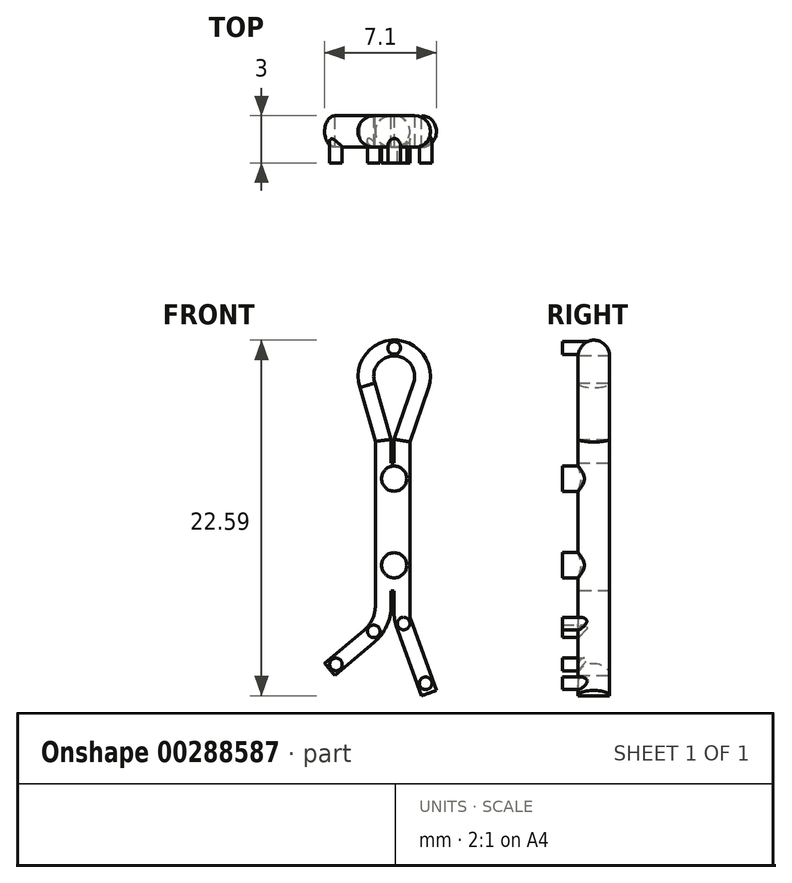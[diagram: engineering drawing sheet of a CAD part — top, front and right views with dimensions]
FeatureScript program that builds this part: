
annotation { "Feature Type Name" : "Feature", "Feature Type Description" : "" }
export const myFeature = defineFeature(function(context is Context, id is Id, definition is map)
    precondition{}
    {
        {
            var Q0;
            Q0=qCreatedBy(makeId("Top.planeOp"),FACE);
            var sketch = newSketch(context, id + "F0", { "sketchPlane" : qUnion([Q0])});
            skLineSegment(sketch, "E0", {"start": v(0, -1) * mm, "end": v(0, 1) * mm});
            skArc(sketch, "E1", {"start": v(0, -1) * mm, "mid": v(1, 0) * mm, "end": v(0, 1) * mm});
            skSolve(sketch);
        }
        {
            var Q0;
            Q0=qCreatedBy(makeId("Front.planeOp"),FACE);
            var sketch = newSketch(context, id + "F1", { "sketchPlane" : qUnion([Q0])});
            skLineSegment(sketch, "E2", {"start": v(0, 0) * mm, "end": v(0, 10) * mm});
            skLineSegment(sketch, "E3", {"start": v(0, 10) * mm, "end": v(1.23, 13.58) * mm});
            skLineSegment(sketch, "E4", {"start": v(-1.23, 13.58) * mm, "end": v(-0.2, 10) * mm});
            skLineSegment(sketch, "E5", {"start": v(-0.2, 10) * mm, "end": v(-0.2, 0) * mm});
            skArc(sketch, "E6", {"start": v(1.23, 13.58) * mm, "mid": v(0, 15.3) * mm, "end": v(-1.23, 13.58) * mm});
            skSolve(sketch);
        }
        {
            var Q0;
            Q0=makeQuery(id+"F0.imprint","IMPRINT",FACE,{"disambiguationData":[TD([[makeQuery(id+"F0.imprint","IMPRINT",EDGE,{"derivedFrom":sQuery(id+"F0.wireOp",EDGE,"E0")}),-1.0]])]});
            var Q1;
            Q1=sQuery(id+"F1.wireOp",EDGE,"E2");
            var Q2;
            Q2=sQuery(id+"F1.wireOp",EDGE,"E3");
            var Q3;
            Q3=sQuery(id+"F1.wireOp",EDGE,"E6");
            var Q4;
            Q4=sQuery(id+"F1.wireOp",EDGE,"E4");
            var Q5;
            Q5=sQuery(id+"F1.wireOp",EDGE,"E5");
            sweep(context, id + "F2", {"profiles" : qUnion([Q0]), "path" : qUnion([Q1, Q2, Q3, Q4, Q5])});
        }
        {
            var Q0;
            Q0=qCreatedBy(makeId("Front.planeOp"),FACE);
            var sketch = newSketch(context, id + "F3", { "sketchPlane" : qUnion([Q0])});
            skLineSegment(sketch, "E7", {"start": v(0, 0) * mm, "end": v(0, -1.15) * mm});
            skLineSegment(sketch, "E8", {"start": v(0.12, -1.83) * mm, "end": v(1.74, -6.3) * mm});
            skPoint(sketch, "E9.visualSharp", {"position": v(0, -1.5) * mm});
            skArc(sketch, "E9.filletArc", {"start": v(0, -1.15) * mm, "mid": v(0.03, -1.5) * mm, "end": v(0.12, -1.83) * mm});
            skSolve(sketch);
        }
        {
            var Q0;
            Q0=qSketchRegion(id+"F0",true);
            var Q1;
            Q1=sQuery(id+"F3.wireOp",EDGE,"E7");
            var Q2;
            Q2=sQuery(id+"F3.wireOp",EDGE,"E9.filletArc");
            var Q3;
            Q3=sQuery(id+"F3.wireOp",EDGE,"E8");
            sweep(context, id + "F4", {"operationType" : NewBodyOperationType.ADD, "profiles" : qUnion([Q0]), "path" : qUnion([Q1, Q2, Q3])});
        }
        {
            var Q0;
            Q0=qCreatedBy(makeId("Front.planeOp"),FACE);
            var sketch = newSketch(context, id + "F5", { "sketchPlane" : qUnion([Q0])});
            skLineSegment(sketch, "E10", {"start": v(-0.2, 0) * mm, "end": v(-0.2, -0.6) * mm});
            skLineSegment(sketch, "E11", {"start": v(-1.27, -2.9) * mm, "end": v(-3.78, -5) * mm});
            skPoint(sketch, "E12.orphan", {"position": v(-0.2, -1) * mm});
            skPoint(sketch, "E13.visualSharp", {"position": v(-0.2, -2) * mm});
            skArc(sketch, "E13.filletArc", {"start": v(-1.27, -2.9) * mm, "mid": v(-0.48, -1.87) * mm, "end": v(-0.2, -0.6) * mm});
            skSolve(sketch);
        }
        {
            var Q0;
            Q0=makeQuery(id+"F2.opSweep","CAP_FACE",FACE,{"disambiguationData":[OSD([sQuery(id+"F0.wireOp",EDGE,"E0"),sQuery(id+"F0.wireOp",EDGE,"E1"),sQuery(id+"F1.wireOp",VERTEX,"E5.end")])],"isStart":false});
            var Q1;
            Q1=sQuery(id+"F5.wireOp",EDGE,"E10");
            var Q2;
            Q2=sQuery(id+"F5.wireOp",EDGE,"E13.filletArc");
            var Q3;
            Q3=sQuery(id+"F5.wireOp",EDGE,"E11");
            sweep(context, id + "F6", {"operationType" : NewBodyOperationType.ADD, "profiles" : qUnion([Q0]), "path" : qUnion([Q1, Q2, Q3])});
        }
        {
            var Q0;
            {var subQ0=sQuery(id+"F0.wireOp",EDGE,"E0");Q0=makeQuery(id+"F4.boolean.opBoolean","MERGE",FACE,{"derivedFrom":[makeQuery(id+"F2.opSweep","SWEPT_FACE",FACE,{"disambiguationData":[OSD([subQ0,sQuery(id+"F1.wireOp",EDGE,"E2")])]}),makeQuery(id+"F4.opSweep","SWEPT_FACE",FACE,{"disambiguationData":[OSD([subQ0,sQuery(id+"F3.wireOp",EDGE,"E7")])]})]});}
            var sketch = newSketch(context, id + "F7", { "sketchPlane" : qUnion([Q0])});
            skLineSegment(sketch, "E14.bottom", {"start": v(-1, 8.5) * mm, "end": v(1, 8.5) * mm});
            skLineSegment(sketch, "E14.top", {"start": v(-1, 0.35) * mm, "end": v(1, 0.35) * mm});
            skLineSegment(sketch, "E14.left", {"start": v(-1, 8.5) * mm, "end": v(-1, 0.35) * mm});
            skLineSegment(sketch, "E14.right", {"start": v(1, 8.5) * mm, "end": v(1, 0.35) * mm});
            skSolve(sketch);
        }
        {
            var Q0;
            Q0=qSketchRegion(id+"F7",true);
            extrude(context, id + "F8", {"entities" : qUnion([Q0]), "operationType" : NewBodyOperationType.ADD, "endBound" : BoundingType.UP_TO_NEXT, "depth" : 25 * mm});
        }
        {
            var Q0;
            Q0=qCreatedBy(makeId("Front.planeOp"),FACE);
            var sketch = newSketch(context, id + "F9", { "sketchPlane" : qUnion([Q0])});
            skCircle(sketch, "E15", {"center": v(0, 2) * mm, "radius": 0.8 * mm});
            skCircle(sketch, "E16", {"center": v(0, 7.5) * mm, "radius": 0.8 * mm});
            skCircle(sketch, "E17", {"center": v(0.6, -1.7) * mm, "radius": 0.4 * mm});
            skCircle(sketch, "E18", {"center": v(2, -5.5) * mm, "radius": 0.4 * mm});
            skCircle(sketch, "E19", {"center": v(-1.3, -2.2) * mm, "radius": 0.4 * mm});
            skCircle(sketch, "E20", {"center": v(-3.7, -4.3) * mm, "radius": 0.4 * mm});
            skCircle(sketch, "E21", {"center": v(0, 15.8) * mm, "radius": 0.4 * mm});
            skSolve(sketch);
        }
        {
            var Q0;
            Q0=qSketchRegion(id+"F9",true);
            extrude(context, id + "F10", {"entities" : qUnion([Q0]), "operationType" : NewBodyOperationType.ADD, "depth" : 2 * mm});
        }
    });
